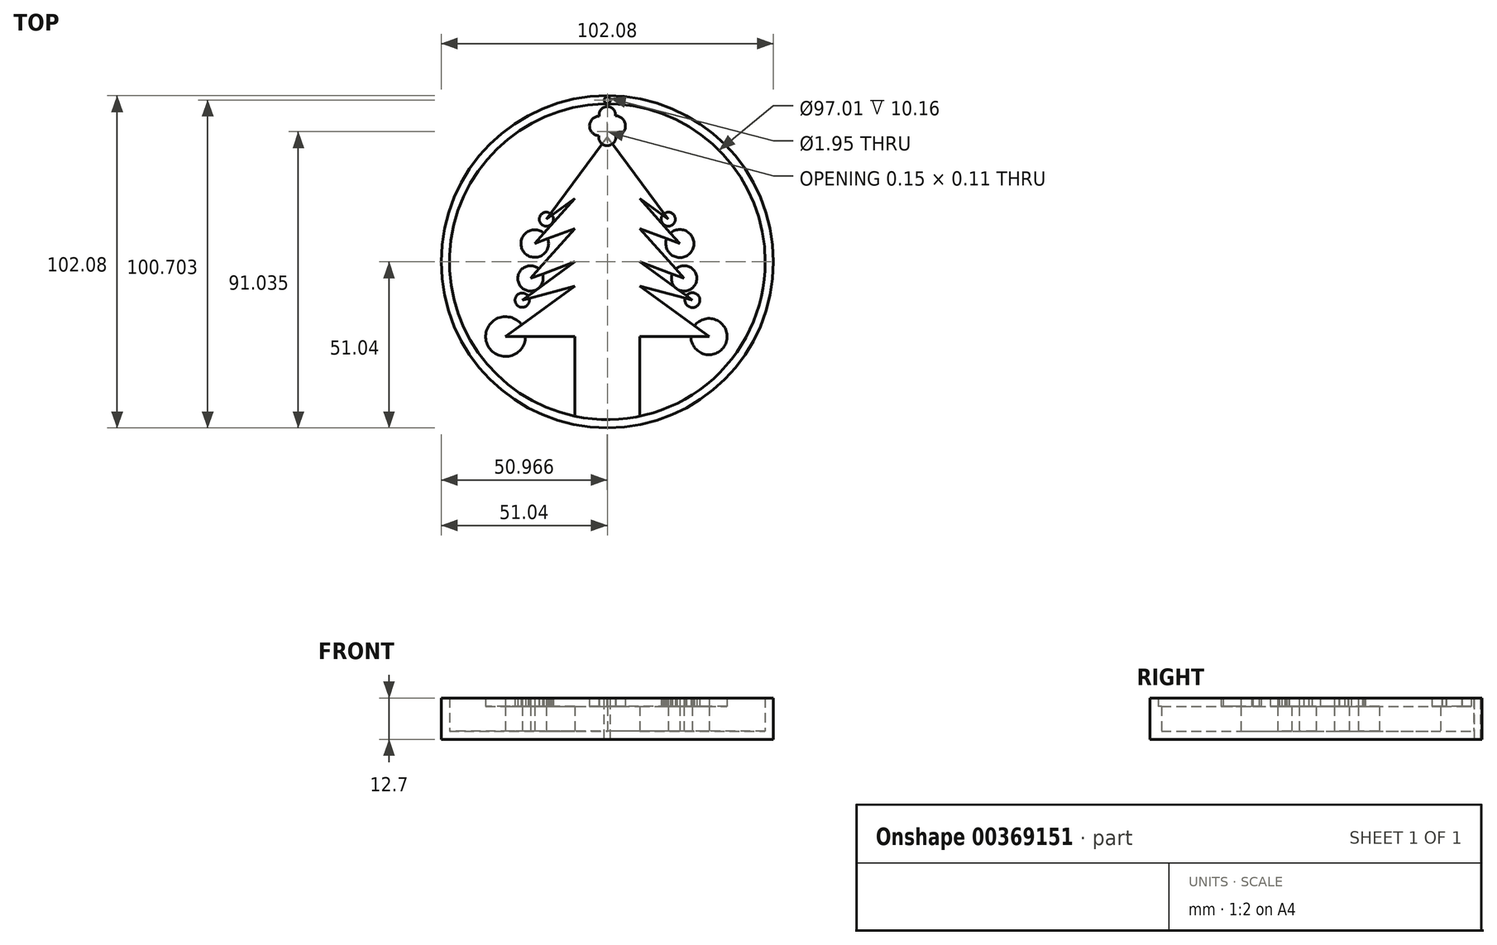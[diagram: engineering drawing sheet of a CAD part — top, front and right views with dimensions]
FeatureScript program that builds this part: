
annotation { "Feature Type Name" : "Feature", "Feature Type Description" : "" }
export const myFeature = defineFeature(function(context is Context, id is Id, definition is map)
    precondition{}
    {
        {
            var Q0;
            Q0=qCreatedBy(makeId("Top.planeOp"),FACE);
            var sketch = newSketch(context, id + "F0", { "sketchPlane" : qUnion([Q0])});
            skCircle(sketch, "E0", {"center": v(0, 0) * mm, "radius": 51.04 * mm});
            skSolve(sketch);
        }
        {
            var Q0;
            Q0 = qSketchRegion(id + "F0", true);
            extrude(context, id + "F1", {"entities" : qUnion([Q0]), "depth" : 12.7 * mm});
        }
        {
            var Q0;
            Q0=makeQuery(id+"F1.opExtrude","CAP_FACE",FACE,{"disambiguationData":[OSD([sQuery(id+"F0.wireOp",EDGE,"E0")])],"isStart":false});
            shell(context, id + "F2", {"entities" : qUnion([Q0]), "thickness" : 2.54 * mm});
        }
        {
            var Q0;
            {var subQ0=sQuery(id+"F0.wireOp",EDGE,"E0");Q0=makeQuery(id+"F2.opShell","OFFSET_FACE",FACE,{"disambiguationData":[OSD([subQ0]),TDD([makeQuery(id+"F1.opExtrude","CAP_FACE",FACE,{"disambiguationData":[OSD([subQ0])],"isStart":true})])]});}
            var sketch = newSketch(context, id + "F3", { "sketchPlane" : qUnion([Q0])});
            skLineSegment(sketch, "E1", {"start": v(0, -48.5) * mm, "end": v(0, 48.5) * mm, "construction": true});
            skLineSegment(sketch, "E2", {"start": v(-9.96, -47.47) * mm, "end": v(-9.96, -23) * mm});
            skLineSegment(sketch, "E3", {"start": v(-9.96, -23) * mm, "end": v(-31.26, -23) * mm});
            skLineSegment(sketch, "E4", {"start": v(-31.26, -23) * mm, "end": v(-9.96, -7.47) * mm});
            skLineSegment(sketch, "E5", {"start": v(-9.96, -7.47) * mm, "end": v(-26.15, -11.8) * mm});
            skLineSegment(sketch, "E6", {"start": v(-26.15, -11.8) * mm, "end": v(-9.96, 0) * mm});
            skLineSegment(sketch, "E7", {"start": v(-9.96, 0) * mm, "end": v(-23.6, -5.11) * mm});
            skLineSegment(sketch, "E8", {"start": v(-23.6, -5.11) * mm, "end": v(-9.96, 10.22) * mm});
            skLineSegment(sketch, "E9", {"start": v(-9.96, 10.22) * mm, "end": v(-22.28, 5.6) * mm});
            skLineSegment(sketch, "E10", {"start": v(-22.28, 5.6) * mm, "end": v(-9.96, 19.46) * mm});
            skLineSegment(sketch, "E11", {"start": v(-9.96, 19.46) * mm, "end": v(-18.73, 13.07) * mm});
            skLineSegment(sketch, "E12", {"start": v(-18.73, 13.07) * mm, "end": v(0, 38.33) * mm});
            skLineSegment(sketch, "E13.MirrorCS", {"start": v(18.73, 13.07) * mm, "end": v(0, 38.33) * mm});
            skLineSegment(sketch, "E14.MirrorCS", {"start": v(9.96, 19.46) * mm, "end": v(18.73, 13.07) * mm});
            skLineSegment(sketch, "E15.MirrorCS", {"start": v(22.28, 5.6) * mm, "end": v(9.96, 19.46) * mm});
            skLineSegment(sketch, "E16.MirrorCS", {"start": v(9.96, 10.22) * mm, "end": v(22.28, 5.6) * mm});
            skLineSegment(sketch, "E17.MirrorCS", {"start": v(23.6, -5.11) * mm, "end": v(9.96, 10.22) * mm});
            skLineSegment(sketch, "E18.MirrorCS", {"start": v(9.96, 0) * mm, "end": v(23.6, -5.11) * mm});
            skLineSegment(sketch, "E19.MirrorCS", {"start": v(26.15, -11.8) * mm, "end": v(9.96, 0) * mm});
            skLineSegment(sketch, "E20.MirrorCS", {"start": v(9.96, -7.47) * mm, "end": v(26.15, -11.8) * mm});
            skLineSegment(sketch, "E21.MirrorCS", {"start": v(31.26, -23) * mm, "end": v(9.96, -7.47) * mm});
            skLineSegment(sketch, "E22.MirrorCS", {"start": v(9.96, -23) * mm, "end": v(31.26, -23) * mm});
            skLineSegment(sketch, "E23.MirrorCS", {"start": v(9.96, -47.47) * mm, "end": v(9.96, -23) * mm});
            skSolve(sketch);
        }
        {
            var Q0;
            {var subQ1=sQuery(id+"F3.wireOp",EDGE,"E2");Q0=makeQuery(id+"F3.imprint","IMPRINT",FACE,{"disambiguationData":[TD([[makeQuery(id+"F3.imprint","IMPRINT",EDGE,{"derivedFrom":subQ1}),-1.0]])]});}
            extrude(context, id + "F4", {"entities" : qUnion([Q0]), "operationType" : NewBodyOperationType.ADD, "depth" : 7.62 * mm});
        }
        {
            var Q0;
            Q0=makeQuery(id+"F4.opExtrude","CAP_FACE",FACE,{"disambiguationData":[OSD([sQuery(id+"F0.wireOp",EDGE,"E0"),sQuery(id+"F3.wireOp",EDGE,"E2"),sQuery(id+"F3.wireOp",EDGE,"E3"),sQuery(id+"F3.wireOp",EDGE,"E4"),sQuery(id+"F3.wireOp",EDGE,"E5"),sQuery(id+"F3.wireOp",EDGE,"E6"),sQuery(id+"F3.wireOp",EDGE,"E7"),sQuery(id+"F3.wireOp",EDGE,"E8"),sQuery(id+"F3.wireOp",EDGE,"E9"),sQuery(id+"F3.wireOp",EDGE,"E10"),sQuery(id+"F3.wireOp",EDGE,"E11"),sQuery(id+"F3.wireOp",EDGE,"E12"),sQuery(id+"F3.wireOp",EDGE,"E13.MirrorCS"),sQuery(id+"F3.wireOp",EDGE,"E14.MirrorCS"),sQuery(id+"F3.wireOp",EDGE,"E15.MirrorCS"),sQuery(id+"F3.wireOp",EDGE,"E16.MirrorCS"),sQuery(id+"F3.wireOp",EDGE,"E17.MirrorCS"),sQuery(id+"F3.wireOp",EDGE,"E18.MirrorCS"),sQuery(id+"F3.wireOp",EDGE,"E19.MirrorCS"),sQuery(id+"F3.wireOp",EDGE,"E20.MirrorCS"),sQuery(id+"F3.wireOp",EDGE,"E21.MirrorCS"),sQuery(id+"F3.wireOp",EDGE,"E22.MirrorCS"),sQuery(id+"F3.wireOp",EDGE,"E23.MirrorCS")])],"isStart":false});
            var sketch = newSketch(context, id + "F5", { "sketchPlane" : qUnion([Q0])});
            skCircle(sketch, "E24", {"center": v(18.73, 13.07) * mm, "radius": 2.17 * mm});
            skCircle(sketch, "E25", {"center": v(22.28, 5.6) * mm, "radius": 4.31 * mm});
            skCircle(sketch, "E26", {"center": v(23.6, -5.11) * mm, "radius": 3.9 * mm});
            skCircle(sketch, "E27", {"center": v(26.15, -11.8) * mm, "radius": 2.3 * mm});
            skCircle(sketch, "E28", {"center": v(31.26, -23) * mm, "radius": 5.57 * mm});
            skCircle(sketch, "E29", {"center": v(-18.73, 13.07) * mm, "radius": 2.17 * mm});
            skCircle(sketch, "E30", {"center": v(-22.28, 5.6) * mm, "radius": 4.25 * mm});
            skCircle(sketch, "E31", {"center": v(-23.6, -5.11) * mm, "radius": 3.9 * mm});
            skCircle(sketch, "E32", {"center": v(-26.15, -11.8) * mm, "radius": 2.2 * mm});
            skCircle(sketch, "E33", {"center": v(-31.26, -23) * mm, "radius": 6.12 * mm});
            skCircle(sketch, "E34", {"center": v(0, 45.18) * mm, "radius": 2.5 * mm});
            skCircle(sketch, "E35", {"center": v(0, 42.68) * mm, "radius": 2.64 * mm});
            skCircle(sketch, "E36", {"center": v(0, 40.04) * mm, "radius": 3 * mm});
            skCircle(sketch, "E37", {"center": v(2.47, 41.75) * mm, "radius": 3.12 * mm});
            skCircle(sketch, "E38", {"center": v(-2.47, 41.75) * mm, "radius": 3 * mm});
            skCircle(sketch, "E39", {"center": v(0, 38.33) * mm, "radius": 2.65 * mm});
            skSolve(sketch);
        }
        {
            var Q0;
            {var subQ0=sQuery(id+"F5.wireOp",EDGE,"E33");var subQ1=makeQuery(id+"F4.opExtrude","CAP_EDGE",EDGE,{"disambiguationData":[OSD([sQuery(id+"F3.wireOp",EDGE,"E3")])],"isStart":false});var subQ2=makeQuery(id+"F5.imprint","INTERSECT",VERTEX,{"derivedFrom":[subQ1,subQ0]});Q0=makeQuery(id+"F5.imprint","IMPRINT",FACE,{"disambiguationData":[TD([[makeQuery(id+"F5.imprint","IMPRINT",EDGE,{"disambiguationData":[TD([[subQ2,1.0]])],"derivedFrom":subQ0}),1.0]])]});}
            var Q1;
            {var subQ0=sQuery(id+"F5.wireOp",EDGE,"E32");var subQ1=makeQuery(id+"F4.opExtrude","CAP_EDGE",EDGE,{"disambiguationData":[OSD([sQuery(id+"F3.wireOp",EDGE,"E5")])],"isStart":false});var subQ2=makeQuery(id+"F5.imprint","INTERSECT",VERTEX,{"derivedFrom":[subQ1,subQ0]});Q1=makeQuery(id+"F5.imprint","IMPRINT",FACE,{"disambiguationData":[TD([[makeQuery(id+"F5.imprint","IMPRINT",EDGE,{"disambiguationData":[TD([[subQ2,1.0]])],"derivedFrom":subQ0}),1.0]])]});}
            var Q2;
            {var subQ0=sQuery(id+"F5.wireOp",EDGE,"E31");var subQ1=makeQuery(id+"F4.opExtrude","CAP_EDGE",EDGE,{"disambiguationData":[OSD([sQuery(id+"F3.wireOp",EDGE,"E8")])],"isStart":false});var subQ2=makeQuery(id+"F5.imprint","INTERSECT",VERTEX,{"derivedFrom":[subQ1,subQ0]});Q2=makeQuery(id+"F5.imprint","IMPRINT",FACE,{"disambiguationData":[TD([[makeQuery(id+"F5.imprint","IMPRINT",EDGE,{"disambiguationData":[TD([[subQ2,-1.0]])],"derivedFrom":subQ0}),1.0]])]});}
            var Q3;
            {var subQ0=sQuery(id+"F5.wireOp",EDGE,"E30");var subQ1=makeQuery(id+"F4.opExtrude","CAP_EDGE",EDGE,{"disambiguationData":[OSD([sQuery(id+"F3.wireOp",EDGE,"E9")])],"isStart":false});var subQ2=makeQuery(id+"F5.imprint","INTERSECT",VERTEX,{"derivedFrom":[subQ1,subQ0]});Q3=makeQuery(id+"F5.imprint","IMPRINT",FACE,{"disambiguationData":[TD([[makeQuery(id+"F5.imprint","IMPRINT",EDGE,{"disambiguationData":[TD([[subQ2,1.0]])],"derivedFrom":subQ0}),1.0]])]});}
            var Q4;
            {var subQ0=sQuery(id+"F5.wireOp",EDGE,"E29");var subQ1=makeQuery(id+"F4.opExtrude","CAP_EDGE",EDGE,{"disambiguationData":[OSD([sQuery(id+"F3.wireOp",EDGE,"E11")])],"isStart":false});var subQ2=makeQuery(id+"F5.imprint","INTERSECT",VERTEX,{"derivedFrom":[subQ1,subQ0]});Q4=makeQuery(id+"F5.imprint","IMPRINT",FACE,{"disambiguationData":[TD([[makeQuery(id+"F5.imprint","IMPRINT",EDGE,{"disambiguationData":[TD([[subQ2,1.0]])],"derivedFrom":subQ0}),1.0]])]});}
            var Q5;
            {var subQ0=sQuery(id+"F5.wireOp",EDGE,"E24");var subQ1=makeQuery(id+"F4.opExtrude","CAP_EDGE",EDGE,{"disambiguationData":[OSD([sQuery(id+"F3.wireOp",EDGE,"E13.MirrorCS")])],"isStart":false});var subQ2=makeQuery(id+"F5.imprint","INTERSECT",VERTEX,{"derivedFrom":[subQ1,subQ0]});Q5=makeQuery(id+"F5.imprint","IMPRINT",FACE,{"disambiguationData":[TD([[makeQuery(id+"F5.imprint","IMPRINT",EDGE,{"disambiguationData":[TD([[subQ2,1.0]])],"derivedFrom":subQ0}),1.0]])]});}
            var Q6;
            {var subQ0=sQuery(id+"F5.wireOp",EDGE,"E25");var subQ1=makeQuery(id+"F4.opExtrude","CAP_EDGE",EDGE,{"disambiguationData":[OSD([sQuery(id+"F3.wireOp",EDGE,"E15.MirrorCS")])],"isStart":false});var subQ2=makeQuery(id+"F5.imprint","INTERSECT",VERTEX,{"derivedFrom":[subQ1,subQ0]});Q6=makeQuery(id+"F5.imprint","IMPRINT",FACE,{"disambiguationData":[TD([[makeQuery(id+"F5.imprint","IMPRINT",EDGE,{"disambiguationData":[TD([[subQ2,1.0]])],"derivedFrom":subQ0}),1.0]])]});}
            var Q7;
            {var subQ0=makeQuery(id+"F4.opExtrude","CAP_EDGE",EDGE,{"disambiguationData":[OSD([sQuery(id+"F3.wireOp",EDGE,"E18.MirrorCS")])],"isStart":false});var subQ3=sQuery(id+"F5.wireOp",EDGE,"E26");var subQ5=makeQuery(id+"F5.imprint","INTERSECT",VERTEX,{"derivedFrom":[subQ0,subQ3]});Q7=makeQuery(id+"F5.imprint","IMPRINT",FACE,{"disambiguationData":[TD([[makeQuery(id+"F5.imprint","IMPRINT",EDGE,{"disambiguationData":[TD([[subQ5,-1.0]])],"derivedFrom":subQ3}),1.0]])]});}
            var Q8;
            {var subQ0=sQuery(id+"F5.wireOp",EDGE,"E27");var subQ1=makeQuery(id+"F4.opExtrude","CAP_EDGE",EDGE,{"disambiguationData":[OSD([sQuery(id+"F3.wireOp",EDGE,"E19.MirrorCS")])],"isStart":false});var subQ2=makeQuery(id+"F5.imprint","INTERSECT",VERTEX,{"derivedFrom":[subQ1,subQ0]});Q8=makeQuery(id+"F5.imprint","IMPRINT",FACE,{"disambiguationData":[TD([[makeQuery(id+"F5.imprint","IMPRINT",EDGE,{"disambiguationData":[TD([[subQ2,1.0]])],"derivedFrom":subQ0}),1.0]])]});}
            var Q9;
            {var subQ0=sQuery(id+"F5.wireOp",EDGE,"E28");var subQ1=makeQuery(id+"F4.opExtrude","CAP_EDGE",EDGE,{"disambiguationData":[OSD([sQuery(id+"F3.wireOp",EDGE,"E21.MirrorCS")])],"isStart":false});var subQ2=makeQuery(id+"F5.imprint","INTERSECT",VERTEX,{"derivedFrom":[subQ1,subQ0]});Q9=makeQuery(id+"F5.imprint","IMPRINT",FACE,{"disambiguationData":[TD([[makeQuery(id+"F5.imprint","IMPRINT",EDGE,{"disambiguationData":[TD([[subQ2,1.0]])],"derivedFrom":subQ0}),1.0]])]});}
            var Q10;
            {var subQ0=sQuery(id+"F5.wireOp",EDGE,"E37");var subQ1=sQuery(id+"F5.wireOp",EDGE,"E34");var subQ2=makeQuery(id+"F5.imprint","INTERSECT",VERTEX,{"disambiguationData":[OD(0.0)],"derivedFrom":[subQ1,subQ0]});Q10=makeQuery(id+"F5.imprint","IMPRINT",FACE,{"disambiguationData":[TD([[makeQuery(id+"F5.imprint","IMPRINT",EDGE,{"disambiguationData":[TD([[subQ2,1.0]])],"derivedFrom":subQ1}),-1.0]])]});}
            var Q11;
            {var subQ0=sQuery(id+"F5.wireOp",EDGE,"E38");var subQ1=sQuery(id+"F5.wireOp",EDGE,"E34");var subQ2=makeQuery(id+"F5.imprint","INTERSECT",VERTEX,{"disambiguationData":[OD(0.0)],"derivedFrom":[subQ1,subQ0]});Q11=makeQuery(id+"F5.imprint","IMPRINT",FACE,{"disambiguationData":[TD([[makeQuery(id+"F5.imprint","IMPRINT",EDGE,{"disambiguationData":[TD([[subQ2,1.0]])],"derivedFrom":subQ1}),1.0]])]});}
            var Q12;
            {var subQ0=sQuery(id+"F5.wireOp",EDGE,"E38");var subQ1=sQuery(id+"F5.wireOp",EDGE,"E34");var subQ2=makeQuery(id+"F5.imprint","INTERSECT",VERTEX,{"disambiguationData":[OD(0.0)],"derivedFrom":[subQ1,subQ0]});Q12=makeQuery(id+"F5.imprint","IMPRINT",FACE,{"disambiguationData":[TD([[makeQuery(id+"F5.imprint","IMPRINT",EDGE,{"disambiguationData":[TD([[subQ2,-1.0]])],"derivedFrom":subQ1}),-1.0]])]});}
            var Q13;
            {var subQ0=sQuery(id+"F5.wireOp",EDGE,"E36");var subQ1=makeQuery(id+"F4.opExtrude","CAP_EDGE",EDGE,{"disambiguationData":[OSD([sQuery(id+"F3.wireOp",EDGE,"E12")])],"isStart":false});var subQ2=makeQuery(id+"F5.imprint","INTERSECT",VERTEX,{"derivedFrom":[subQ1,subQ0]});Q13=makeQuery(id+"F5.imprint","IMPRINT",FACE,{"disambiguationData":[TD([[makeQuery(id+"F5.imprint","IMPRINT",EDGE,{"disambiguationData":[TD([[subQ2,-1.0]])],"derivedFrom":subQ0}),-1.0]])]});}
            var Q14;
            {var subQ0=sQuery(id+"F5.wireOp",EDGE,"E39");var subQ1=sQuery(id+"F5.wireOp",EDGE,"E36");var subQ2=makeQuery(id+"F5.imprint","INTERSECT",VERTEX,{"disambiguationData":[OD(0.0)],"derivedFrom":[subQ1,subQ0]});Q14=makeQuery(id+"F5.imprint","IMPRINT",FACE,{"disambiguationData":[TD([[makeQuery(id+"F5.imprint","IMPRINT",EDGE,{"disambiguationData":[TD([[subQ2,-1.0]])],"derivedFrom":subQ1}),-1.0]])]});}
            var Q15;
            {var subQ0=sQuery(id+"F5.wireOp",EDGE,"E39");var subQ1=sQuery(id+"F5.wireOp",EDGE,"E36");var subQ2=makeQuery(id+"F5.imprint","INTERSECT",VERTEX,{"disambiguationData":[OD(1.0)],"derivedFrom":[subQ1,subQ0]});Q15=makeQuery(id+"F5.imprint","IMPRINT",FACE,{"disambiguationData":[TD([[makeQuery(id+"F5.imprint","IMPRINT",EDGE,{"disambiguationData":[TD([[subQ2,1.0]])],"derivedFrom":subQ1}),-1.0]])]});}
            var Q16;
            {var subQ3=sQuery(id+"F5.wireOp",EDGE,"E39");var subQ6=sQuery(id+"F5.wireOp",EDGE,"E36");var subQ10=makeQuery(id+"F5.imprint","INTERSECT",VERTEX,{"disambiguationData":[OD(0.0)],"derivedFrom":[subQ6,subQ3]});Q16=makeQuery(id+"F5.imprint","IMPRINT",FACE,{"disambiguationData":[TD([[makeQuery(id+"F5.imprint","IMPRINT",EDGE,{"disambiguationData":[TD([[subQ10,-1.0]])],"derivedFrom":subQ6}),1.0]])]});}
            var Q17;
            {var subQ0=sQuery(id+"F5.wireOp",EDGE,"E36");var subQ1=makeQuery(id+"F4.opExtrude","CAP_EDGE",EDGE,{"disambiguationData":[OSD([sQuery(id+"F3.wireOp",EDGE,"E12")])],"isStart":false});var subQ2=makeQuery(id+"F5.imprint","INTERSECT",VERTEX,{"derivedFrom":[subQ1,subQ0]});Q17=makeQuery(id+"F5.imprint","IMPRINT",FACE,{"disambiguationData":[TD([[makeQuery(id+"F5.imprint","IMPRINT",EDGE,{"disambiguationData":[TD([[subQ2,-1.0]])],"derivedFrom":subQ0}),1.0]])]});}
            var Q18;
            {var subQ0=sQuery(id+"F5.wireOp",EDGE,"E39");var subQ1=sQuery(id+"F5.wireOp",EDGE,"E35");var subQ2=makeQuery(id+"F5.imprint","INTERSECT",VERTEX,{"disambiguationData":[OD(0.0)],"derivedFrom":[subQ1,subQ0]});Q18=makeQuery(id+"F5.imprint","IMPRINT",FACE,{"disambiguationData":[TD([[makeQuery(id+"F5.imprint","IMPRINT",EDGE,{"disambiguationData":[TD([[subQ2,-1.0]])],"derivedFrom":subQ1}),-1.0]])]});}
            var Q19;
            {var subQ0=sQuery(id+"F5.wireOp",EDGE,"E36");var subQ1=sQuery(id+"F5.wireOp",EDGE,"E35");var subQ2=makeQuery(id+"F5.imprint","INTERSECT",VERTEX,{"disambiguationData":[OD(0.0)],"derivedFrom":[subQ1,subQ0]});Q19=makeQuery(id+"F5.imprint","IMPRINT",FACE,{"disambiguationData":[TD([[makeQuery(id+"F5.imprint","IMPRINT",EDGE,{"disambiguationData":[TD([[subQ2,-1.0]])],"derivedFrom":subQ1}),-1.0]])]});}
            var Q20;
            {var subQ1=sQuery(id+"F5.wireOp",EDGE,"E34");var subQ5=sQuery(id+"F5.wireOp",EDGE,"E36");var subQ9=makeQuery(id+"F5.imprint","INTERSECT",VERTEX,{"disambiguationData":[OD(0.0)],"derivedFrom":[subQ1,subQ5]});Q20=makeQuery(id+"F5.imprint","IMPRINT",FACE,{"disambiguationData":[TD([[makeQuery(id+"F5.imprint","IMPRINT",EDGE,{"disambiguationData":[TD([[subQ9,-1.0]])],"derivedFrom":subQ1}),-1.0]])]});}
            var Q21;
            {var subQ0=sQuery(id+"F5.wireOp",EDGE,"E35");var subQ1=sQuery(id+"F5.wireOp",EDGE,"E34");var subQ2=makeQuery(id+"F5.imprint","INTERSECT",VERTEX,{"disambiguationData":[OD(0.0)],"derivedFrom":[subQ1,subQ0]});Q21=makeQuery(id+"F5.imprint","IMPRINT",FACE,{"disambiguationData":[TD([[makeQuery(id+"F5.imprint","IMPRINT",EDGE,{"disambiguationData":[TD([[subQ2,-1.0]])],"derivedFrom":subQ1}),-1.0]])]});}
            var Q22;
            {var subQ5=sQuery(id+"F5.wireOp",EDGE,"E35");var subQ6=sQuery(id+"F5.wireOp",EDGE,"E34");var subQ7=makeQuery(id+"F5.imprint","INTERSECT",VERTEX,{"disambiguationData":[OD(0.0)],"derivedFrom":[subQ6,subQ5]});Q22=makeQuery(id+"F5.imprint","IMPRINT",FACE,{"disambiguationData":[TD([[makeQuery(id+"F5.imprint","IMPRINT",EDGE,{"disambiguationData":[TD([[subQ7,-1.0]])],"derivedFrom":subQ6}),1.0]])]});}
            var Q23;
            {var subQ0=sQuery(id+"F5.wireOp",EDGE,"E37");var subQ1=sQuery(id+"F5.wireOp",EDGE,"E35");var subQ2=makeQuery(id+"F5.imprint","INTERSECT",VERTEX,{"disambiguationData":[OD(0.0)],"derivedFrom":[subQ1,subQ0]});Q23=makeQuery(id+"F5.imprint","IMPRINT",FACE,{"disambiguationData":[TD([[makeQuery(id+"F5.imprint","IMPRINT",EDGE,{"disambiguationData":[TD([[subQ2,-1.0]])],"derivedFrom":subQ1}),1.0]])]});}
            var Q24;
            {var subQ5=sQuery(id+"F5.wireOp",EDGE,"E36");var subQ6=sQuery(id+"F5.wireOp",EDGE,"E34");var subQ7=makeQuery(id+"F5.imprint","INTERSECT",VERTEX,{"disambiguationData":[OD(1.0)],"derivedFrom":[subQ6,subQ5]});Q24=makeQuery(id+"F5.imprint","IMPRINT",FACE,{"disambiguationData":[TD([[makeQuery(id+"F5.imprint","IMPRINT",EDGE,{"disambiguationData":[TD([[subQ7,-1.0]])],"derivedFrom":subQ6}),1.0]])]});}
            var Q25;
            {var subQ0=sQuery(id+"F5.wireOp",EDGE,"E36");var subQ1=sQuery(id+"F5.wireOp",EDGE,"E34");var subQ2=makeQuery(id+"F5.imprint","INTERSECT",VERTEX,{"disambiguationData":[OD(1.0)],"derivedFrom":[subQ1,subQ0]});Q25=makeQuery(id+"F5.imprint","IMPRINT",FACE,{"disambiguationData":[TD([[makeQuery(id+"F5.imprint","IMPRINT",EDGE,{"disambiguationData":[TD([[subQ2,-1.0]])],"derivedFrom":subQ1}),-1.0]])]});}
            var Q26;
            {var subQ0=sQuery(id+"F5.wireOp",EDGE,"E37");var subQ1=sQuery(id+"F5.wireOp",EDGE,"E34");var subQ2=makeQuery(id+"F5.imprint","INTERSECT",VERTEX,{"disambiguationData":[OD(0.0)],"derivedFrom":[subQ1,subQ0]});Q26=makeQuery(id+"F5.imprint","IMPRINT",FACE,{"disambiguationData":[TD([[makeQuery(id+"F5.imprint","IMPRINT",EDGE,{"disambiguationData":[TD([[subQ2,1.0]])],"derivedFrom":subQ1}),1.0]])]});}
            var Q27;
            {var subQ1=sQuery(id+"F5.wireOp",EDGE,"E34");var subQ7=sQuery(id+"F5.wireOp",EDGE,"E38");var subQ8=makeQuery(id+"F5.imprint","INTERSECT",VERTEX,{"disambiguationData":[OD(1.0)],"derivedFrom":[subQ1,subQ7]});Q27=makeQuery(id+"F5.imprint","IMPRINT",FACE,{"disambiguationData":[TD([[makeQuery(id+"F5.imprint","IMPRINT",EDGE,{"disambiguationData":[TD([[subQ8,-1.0]])],"derivedFrom":subQ1}),-1.0]])]});}
            var Q28;
            {var subQ0=sQuery(id+"F5.wireOp",EDGE,"E37");var subQ1=sQuery(id+"F5.wireOp",EDGE,"E34");var subQ2=makeQuery(id+"F5.imprint","INTERSECT",VERTEX,{"disambiguationData":[OD(1.0)],"derivedFrom":[subQ1,subQ0]});Q28=makeQuery(id+"F5.imprint","IMPRINT",FACE,{"disambiguationData":[TD([[makeQuery(id+"F5.imprint","IMPRINT",EDGE,{"disambiguationData":[TD([[subQ2,-1.0]])],"derivedFrom":subQ1}),-1.0]])]});}
            var Q29;
            {var subQ0=sQuery(id+"F5.wireOp",EDGE,"E38");var subQ1=sQuery(id+"F5.wireOp",EDGE,"E34");var subQ2=makeQuery(id+"F5.imprint","INTERSECT",VERTEX,{"disambiguationData":[OD(0.0)],"derivedFrom":[subQ1,subQ0]});Q29=makeQuery(id+"F5.imprint","IMPRINT",FACE,{"disambiguationData":[TD([[makeQuery(id+"F5.imprint","IMPRINT",EDGE,{"disambiguationData":[TD([[subQ2,-1.0]])],"derivedFrom":subQ1}),1.0]])]});}
            var Q30;
            {var subQ0=sQuery(id+"F5.wireOp",EDGE,"E39");var subQ1=sQuery(id+"F5.wireOp",EDGE,"E35");var subQ2=makeQuery(id+"F5.imprint","INTERSECT",VERTEX,{"disambiguationData":[OD(0.0)],"derivedFrom":[subQ1,subQ0]});Q30=makeQuery(id+"F5.imprint","IMPRINT",FACE,{"disambiguationData":[TD([[makeQuery(id+"F5.imprint","IMPRINT",EDGE,{"disambiguationData":[TD([[subQ2,-1.0]])],"derivedFrom":subQ1}),1.0]])]});}
            var Q31;
            {var subQ0=sQuery(id+"F5.wireOp",EDGE,"E37");var subQ1=sQuery(id+"F5.wireOp",EDGE,"E35");var subQ2=makeQuery(id+"F5.imprint","INTERSECT",VERTEX,{"disambiguationData":[OD(1.0)],"derivedFrom":[subQ1,subQ0]});Q31=makeQuery(id+"F5.imprint","IMPRINT",FACE,{"disambiguationData":[TD([[makeQuery(id+"F5.imprint","IMPRINT",EDGE,{"disambiguationData":[TD([[subQ2,-1.0]])],"derivedFrom":subQ1}),1.0]])]});}
            var Q32;
            {var subQ0=sQuery(id+"F5.wireOp",EDGE,"E38");var subQ1=sQuery(id+"F5.wireOp",EDGE,"E35");var subQ2=makeQuery(id+"F5.imprint","INTERSECT",VERTEX,{"disambiguationData":[OD(1.0)],"derivedFrom":[subQ1,subQ0]});Q32=makeQuery(id+"F5.imprint","IMPRINT",FACE,{"disambiguationData":[TD([[makeQuery(id+"F5.imprint","IMPRINT",EDGE,{"disambiguationData":[TD([[subQ2,-1.0]])],"derivedFrom":subQ1}),1.0]])]});}
            var Q33;
            {var subQ0=sQuery(id+"F5.wireOp",EDGE,"E38");var subQ1=sQuery(id+"F5.wireOp",EDGE,"E35");var subQ2=makeQuery(id+"F5.imprint","INTERSECT",VERTEX,{"disambiguationData":[OD(1.0)],"derivedFrom":[subQ1,subQ0]});Q33=makeQuery(id+"F5.imprint","IMPRINT",FACE,{"disambiguationData":[TD([[makeQuery(id+"F5.imprint","IMPRINT",EDGE,{"disambiguationData":[TD([[subQ2,-1.0]])],"derivedFrom":subQ1}),-1.0]])]});}
            var Q34;
            {var subQ0=sQuery(id+"F5.wireOp",EDGE,"E39");var subQ1=sQuery(id+"F5.wireOp",EDGE,"E35");var subQ2=makeQuery(id+"F5.imprint","INTERSECT",VERTEX,{"disambiguationData":[OD(1.0)],"derivedFrom":[subQ1,subQ0]});Q34=makeQuery(id+"F5.imprint","IMPRINT",FACE,{"disambiguationData":[TD([[makeQuery(id+"F5.imprint","IMPRINT",EDGE,{"disambiguationData":[TD([[subQ2,-1.0]])],"derivedFrom":subQ1}),-1.0]])]});}
            var Q35;
            {var subQ0=sQuery(id+"F5.wireOp",EDGE,"E37");var subQ1=sQuery(id+"F5.wireOp",EDGE,"E34");var subQ2=makeQuery(id+"F5.imprint","INTERSECT",VERTEX,{"disambiguationData":[OD(1.0)],"derivedFrom":[subQ1,subQ0]});Q35=makeQuery(id+"F5.imprint","IMPRINT",FACE,{"disambiguationData":[TD([[makeQuery(id+"F5.imprint","IMPRINT",EDGE,{"disambiguationData":[TD([[subQ2,-1.0]])],"derivedFrom":subQ1}),1.0]])]});}
            var Q36;
            {var subQ0=sQuery(id+"F5.wireOp",EDGE,"E38");var subQ1=sQuery(id+"F5.wireOp",EDGE,"E36");var subQ2=makeQuery(id+"F5.imprint","INTERSECT",VERTEX,{"disambiguationData":[OD(1.0)],"derivedFrom":[subQ1,subQ0]});Q36=makeQuery(id+"F5.imprint","IMPRINT",FACE,{"disambiguationData":[TD([[makeQuery(id+"F5.imprint","IMPRINT",EDGE,{"disambiguationData":[TD([[subQ2,-1.0]])],"derivedFrom":subQ1}),-1.0]])]});}
            var Q37;
            {var subQ0=sQuery(id+"F5.wireOp",EDGE,"E36");var subQ1=sQuery(id+"F5.wireOp",EDGE,"E34");var subQ2=makeQuery(id+"F5.imprint","INTERSECT",VERTEX,{"disambiguationData":[OD(0.0)],"derivedFrom":[subQ1,subQ0]});Q37=makeQuery(id+"F5.imprint","IMPRINT",FACE,{"disambiguationData":[TD([[makeQuery(id+"F5.imprint","IMPRINT",EDGE,{"disambiguationData":[TD([[subQ2,-1.0]])],"derivedFrom":subQ1}),1.0]])]});}
            var Q38;
            {var subQ0=sQuery(id+"F5.wireOp",EDGE,"E38");var subQ1=sQuery(id+"F5.wireOp",EDGE,"E34");var subQ2=makeQuery(id+"F5.imprint","INTERSECT",VERTEX,{"disambiguationData":[OD(1.0)],"derivedFrom":[subQ1,subQ0]});Q38=makeQuery(id+"F5.imprint","IMPRINT",FACE,{"disambiguationData":[TD([[makeQuery(id+"F5.imprint","IMPRINT",EDGE,{"disambiguationData":[TD([[subQ2,-1.0]])],"derivedFrom":subQ1}),1.0]])]});}
            extrude(context, id + "F6", {"entities" : qUnion([Q0, Q1, Q2, Q3, Q4, Q5, Q6, Q7, Q8, Q9, Q10, Q11, Q12, Q13, Q14, Q15, Q16, Q17, Q18, Q19, Q20, Q21, Q22, Q23, Q24, Q25, Q26, Q27, Q28, Q29, Q30, Q31, Q32, Q33, Q34, Q35, Q36, Q37, Q38]), "depth" : 2.54 * mm});
        }
        {
            var Q0;
            Q0=makeQuery(id+"F1.opExtrude","CAP_FACE",FACE,{"disambiguationData":[OSD([sQuery(id+"F0.wireOp",EDGE,"E0")])],"isStart":false});
            var sketch = newSketch(context, id + "F7", { "sketchPlane" : qUnion([Q0])});
            skCircle(sketch, "E40", {"center": v(0, 49.66) * mm, "radius": 0.98 * mm});
            skSolve(sketch);
        }
        {
            var Q0;
            Q0 = qSketchRegion(id + "F7", true);
            extrude(context, id + "F8", {"entities" : qUnion([Q0]), "operationType" : NewBodyOperationType.REMOVE, "endBound" : BoundingType.THROUGH_ALL, "oppositeDirection" : true, "depth" : 25.4 * mm});
        }
    });
